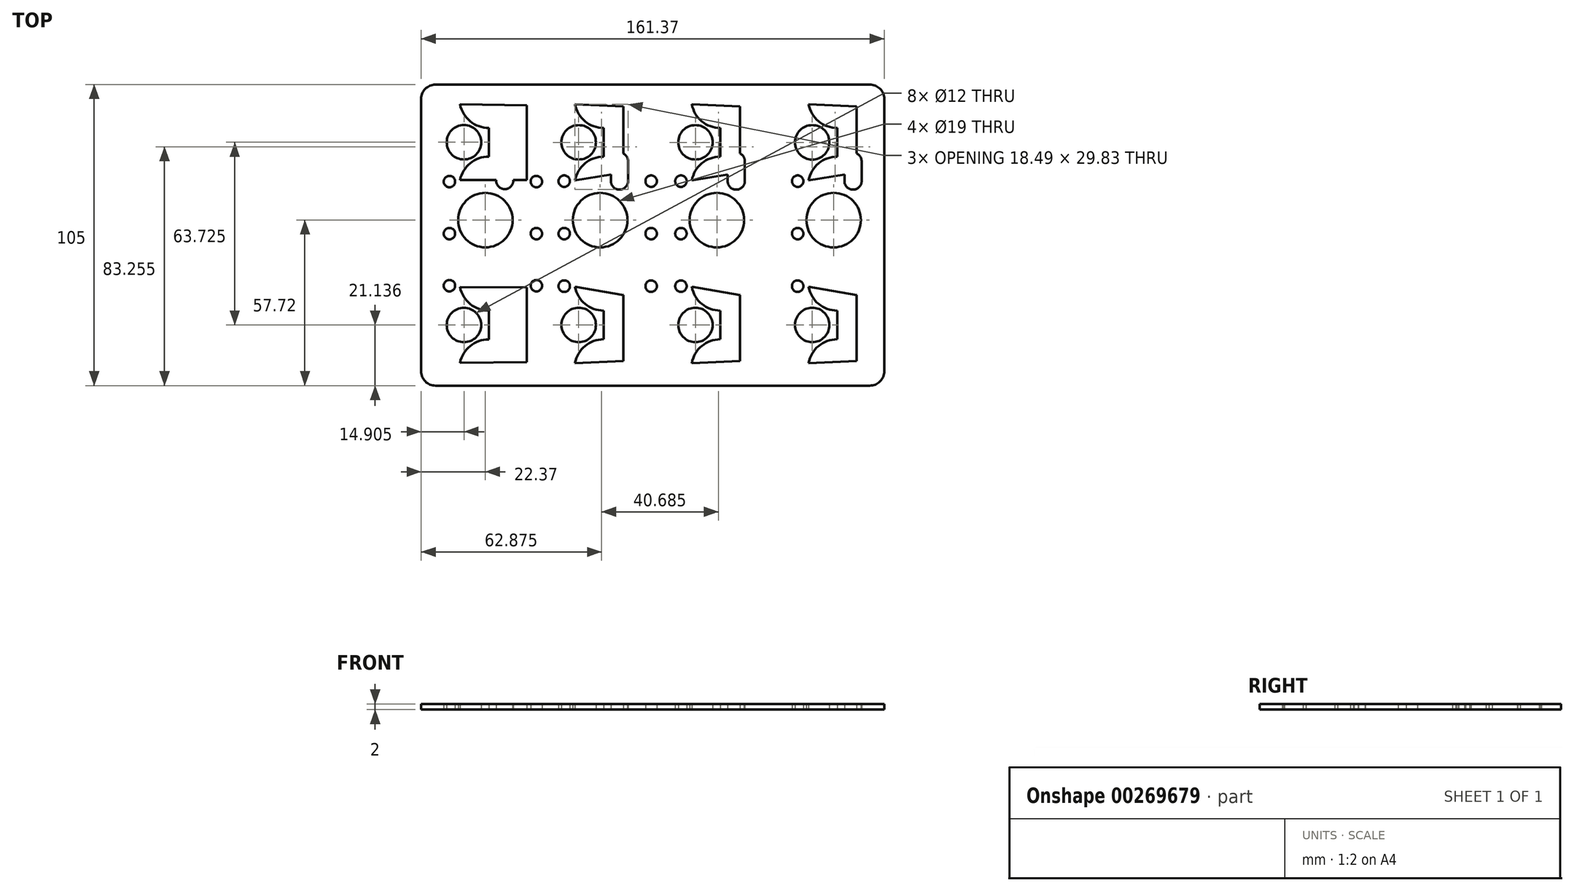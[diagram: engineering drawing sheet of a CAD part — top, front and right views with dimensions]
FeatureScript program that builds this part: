
annotation { "Feature Type Name" : "Feature", "Feature Type Description" : "" }
export const myFeature = defineFeature(function(context is Context, id is Id, definition is map)
    precondition{}
    {
        {
            var Q0;
            Q0=qCreatedBy(makeId("Top.planeOp"),FACE);
            var sketch = newSketch(context, id + "F0", { "sketchPlane" : qUnion([Q0])});
            skLineSegment(sketch, "E0.left", {"start": v(-63.88, 51.14) * mm, "end": v(-63.88, -53.86) * mm});
            skArc(sketch, "E1", {"start": v(-50.35, 44.2) * mm, "mid": v(-46.77, 38.3) * mm, "end": v(-40.26, 36) * mm});
            skLineSegment(sketch, "E2", {"start": v(-40.26, 36) * mm, "end": v(-40.26, 26) * mm});
            skLineSegment(sketch, "E3", {"start": v(-54.06, 31) * mm, "end": v(-19.75, 31) * mm, "construction": true});
            skArc(sketch, "E4.MirrorCS", {"start": v(-50.35, 17.8) * mm, "mid": v(-46.77, 23.7) * mm, "end": v(-40.26, 26) * mm});
            skCircle(sketch, "E5", {"center": v(-44.5, 39.5) * mm, "radius": 1.5 * mm});
            skCircle(sketch, "E6.MirrorC", {"center": v(-44.5, 22.5) * mm, "radius": 1.5 * mm});
            skCircle(sketch, "E7", {"center": v(-48.98, 31) * mm, "radius": 6 * mm});
            skLineSegment(sketch, "E8", {"start": v(-70.35, -0.86) * mm, "end": v(-21.34, -0.86) * mm, "construction": true});
            skCircle(sketch, "E9.MirrorC", {"center": v(-44.5, -24.22) * mm, "radius": 1.5 * mm});
            skArc(sketch, "E10.MirrorCS", {"start": v(-50.35, -19.52) * mm, "mid": v(-46.77, -25.43) * mm, "end": v(-40.26, -27.72) * mm});
            skLineSegment(sketch, "E11.MirrorCS", {"start": v(-40.26, -37.72) * mm, "end": v(-40.26, -27.72) * mm});
            skArc(sketch, "E12.MirrorCS", {"start": v(-50.35, -45.92) * mm, "mid": v(-46.77, -40.02) * mm, "end": v(-40.26, -37.72) * mm});
            skCircle(sketch, "E13.MirrorC", {"center": v(-44.5, -41.22) * mm, "radius": 1.5 * mm});
            skCircle(sketch, "E14.MirrorC", {"center": v(-48.98, -32.72) * mm, "radius": 6 * mm});
            skLineSegment(sketch, "E15", {"start": v(-47.12, -19.26) * mm, "end": v(-47.12, -50.4) * mm, "construction": true});
            skLineSegment(sketch, "E16", {"start": v(-27.05, -19.62) * mm, "end": v(-27.05, -45.62) * mm});
            skLineSegment(sketch, "E17", {"start": v(-27.05, -45.62) * mm, "end": v(-50.35, -45.92) * mm});
            skLineSegment(sketch, "E18", {"start": v(-27.05, -19.62) * mm, "end": v(-50.35, -19.52) * mm});
            skLineSegment(sketch, "E19.MirrorCS", {"start": v(-27.05, 17.9) * mm, "end": v(-50.35, 17.8) * mm});
            skLineSegment(sketch, "E20.MirrorCS", {"start": v(-27.05, 17.9) * mm, "end": v(-27.05, 43.9) * mm});
            skLineSegment(sketch, "E21.MirrorCS", {"start": v(-27.05, 43.9) * mm, "end": v(-50.35, 44.2) * mm});
            skCircle(sketch, "E22", {"center": v(-41.51, 3.86) * mm, "radius": 9.5 * mm});
            skCircle(sketch, "E23", {"center": v(-34.76, 24.59) * mm, "radius": 3 * mm});
            skCircle(sketch, "E24", {"center": v(-34.76, 17.66) * mm, "radius": 3 * mm});
            skLineSegment(sketch, "E25", {"start": v(-31.76, 24.59) * mm, "end": v(-31.76, 17.72) * mm});
            skLineSegment(sketch, "E26", {"start": v(-37.76, 17.66) * mm, "end": v(-37.76, 24.59) * mm});
            skCircle(sketch, "E27", {"center": v(-54.03, -0.86) * mm, "radius": 2 * mm});
            skCircle(sketch, "E28", {"center": v(-54.03, -19.01) * mm, "radius": 2 * mm});
            skCircle(sketch, "E29.MirrorC", {"center": v(-54.03, 17.3) * mm, "radius": 2 * mm});
            skLineSegment(sketch, "E30", {"start": v(-23.88, 51.14) * mm, "end": v(-23.2, 51.14) * mm});
            skLineSegment(sketch, "E31", {"start": v(-23.88, -53.86) * mm, "end": v(-23.34, -53.86) * mm});
            skLineSegment(sketch, "E32", {"start": v(-38.88, -17.7) * mm, "end": v(-38.88, 2.39) * mm, "construction": true});
            skCircle(sketch, "E33.MirrorC", {"center": v(-23.72, -0.86) * mm, "radius": 2 * mm});
            skCircle(sketch, "E34.MirrorC", {"center": v(-23.72, 17.3) * mm, "radius": 2 * mm});
            skCircle(sketch, "E35.MirrorC", {"center": v(-23.72, -19.01) * mm, "radius": 2 * mm});
            skArc(sketch, "E36", {"start": v(-10.25, 44.3) * mm, "mid": v(-6.78, 38.33) * mm, "end": v(-0.27, 35.99) * mm});
            skLineSegment(sketch, "E37", {"start": v(-0.27, 35.99) * mm, "end": v(-0.27, 25.99) * mm});
            skLineSegment(sketch, "E38", {"start": v(-14.06, 30.99) * mm, "end": v(20.24, 30.99) * mm, "construction": true});
            skArc(sketch, "E39.MirrorCS", {"start": v(-10.25, 17.66) * mm, "mid": v(-6.78, 23.65) * mm, "end": v(-0.27, 25.99) * mm});
            skCircle(sketch, "E40", {"center": v(-4.5, 39.49) * mm, "radius": 1.5 * mm});
            skCircle(sketch, "E41.MirrorC", {"center": v(-4.5, 22.49) * mm, "radius": 1.5 * mm});
            skCircle(sketch, "E42", {"center": v(-8.98, 30.99) * mm, "radius": 6 * mm});
            skLineSegment(sketch, "E43", {"start": v(-30.35, -0.86) * mm, "end": v(18.66, -0.86) * mm, "construction": true});
            skCircle(sketch, "E44.MirrorC", {"center": v(-4.5, -24.2) * mm, "radius": 1.5 * mm});
            skArc(sketch, "E45.MirrorCS", {"start": v(-10.25, -19.38) * mm, "mid": v(-6.78, -25.37) * mm, "end": v(-0.27, -27.7) * mm});
            skLineSegment(sketch, "E46.MirrorCS", {"start": v(-0.27, -37.7) * mm, "end": v(-0.27, -27.7) * mm});
            skArc(sketch, "E47.MirrorCS", {"start": v(-10.25, -46.03) * mm, "mid": v(-6.78, -40.05) * mm, "end": v(-0.27, -37.7) * mm});
            skCircle(sketch, "E48.MirrorC", {"center": v(-4.5, -41.2) * mm, "radius": 1.5 * mm});
            skCircle(sketch, "E49.MirrorC", {"center": v(-8.98, -32.7) * mm, "radius": 6 * mm});
            skLineSegment(sketch, "E50", {"start": v(-7.13, -19.44) * mm, "end": v(-7.13, -50.58) * mm, "construction": true});
            skLineSegment(sketch, "E51", {"start": v(6.55, -22.23) * mm, "end": v(6.55, -45.23) * mm});
            skLineSegment(sketch, "E52", {"start": v(6.55, -45.23) * mm, "end": v(-10.25, -46.03) * mm});
            skLineSegment(sketch, "E53", {"start": v(6.55, -22.23) * mm, "end": v(-10.25, -19.38) * mm});
            skLineSegment(sketch, "E54.MirrorCS", {"start": v(6.55, 20.5) * mm, "end": v(-10.25, 17.66) * mm});
            skLineSegment(sketch, "E55.MirrorCS", {"start": v(6.55, 20.5) * mm, "end": v(6.55, 43.5) * mm});
            skLineSegment(sketch, "E56.MirrorCS", {"start": v(6.55, 43.5) * mm, "end": v(-10.25, 44.3) * mm});
            skCircle(sketch, "E57", {"center": v(-1.51, 3.86) * mm, "radius": 9.5 * mm});
            skCircle(sketch, "E58", {"center": v(5.24, 24.4) * mm, "radius": 3 * mm});
            skCircle(sketch, "E59", {"center": v(5.24, 17.48) * mm, "radius": 3 * mm});
            skLineSegment(sketch, "E60", {"start": v(8.24, 24.4) * mm, "end": v(8.24, 17.54) * mm});
            skLineSegment(sketch, "E61", {"start": v(2.24, 17.48) * mm, "end": v(2.24, 24.4) * mm});
            skCircle(sketch, "E62", {"center": v(-14.03, -0.86) * mm, "radius": 2 * mm});
            skCircle(sketch, "E63", {"center": v(-14.03, -19.17) * mm, "radius": 2 * mm});
            skCircle(sketch, "E64.MirrorC", {"center": v(-14.03, 17.45) * mm, "radius": 2 * mm});
            skLineSegment(sketch, "E65", {"start": v(16.12, 51.14) * mm, "end": v(16.8, 51.14) * mm});
            skLineSegment(sketch, "E66", {"start": v(16.12, -53.86) * mm, "end": v(16.66, -53.86) * mm});
            skLineSegment(sketch, "E67", {"start": v(1.12, -28.54) * mm, "end": v(1.12, -8.45) * mm, "construction": true});
            skCircle(sketch, "E68.MirrorC", {"center": v(16.28, -0.86) * mm, "radius": 2 * mm});
            skCircle(sketch, "E69.MirrorC", {"center": v(16.28, 17.45) * mm, "radius": 2 * mm});
            skCircle(sketch, "E70.MirrorC", {"center": v(16.28, -19.17) * mm, "radius": 2 * mm});
            skArc(sketch, "E71", {"start": v(30.44, 44.3) * mm, "mid": v(33.9, 38.33) * mm, "end": v(40.42, 35.99) * mm});
            skLineSegment(sketch, "E72", {"start": v(40.42, 35.99) * mm, "end": v(40.42, 25.99) * mm});
            skLineSegment(sketch, "E73", {"start": v(26.62, 30.99) * mm, "end": v(60.93, 30.99) * mm, "construction": true});
            skArc(sketch, "E74.MirrorCS", {"start": v(30.44, 17.66) * mm, "mid": v(33.9, 23.65) * mm, "end": v(40.42, 25.99) * mm});
            skCircle(sketch, "E75", {"center": v(36.2, 39.49) * mm, "radius": 1.5 * mm});
            skCircle(sketch, "E76.MirrorC", {"center": v(36.2, 22.49) * mm, "radius": 1.5 * mm});
            skCircle(sketch, "E77", {"center": v(31.7, 30.99) * mm, "radius": 6 * mm});
            skLineSegment(sketch, "E78", {"start": v(10.34, -0.86) * mm, "end": v(59.35, -0.86) * mm, "construction": true});
            skCircle(sketch, "E79.MirrorC", {"center": v(36.2, -24.2) * mm, "radius": 1.5 * mm});
            skArc(sketch, "E80.MirrorCS", {"start": v(30.44, -19.38) * mm, "mid": v(33.9, -25.37) * mm, "end": v(40.42, -27.7) * mm});
            skLineSegment(sketch, "E81.MirrorCS", {"start": v(40.42, -37.7) * mm, "end": v(40.42, -27.7) * mm});
            skArc(sketch, "E82.MirrorCS", {"start": v(30.44, -46.03) * mm, "mid": v(33.9, -40.05) * mm, "end": v(40.42, -37.7) * mm});
            skCircle(sketch, "E83.MirrorC", {"center": v(36.2, -41.2) * mm, "radius": 1.5 * mm});
            skCircle(sketch, "E84.MirrorC", {"center": v(31.7, -32.7) * mm, "radius": 6 * mm});
            skLineSegment(sketch, "E85", {"start": v(33.56, -19.44) * mm, "end": v(33.56, -50.58) * mm, "construction": true});
            skLineSegment(sketch, "E86", {"start": v(47.23, -22.23) * mm, "end": v(47.23, -45.23) * mm});
            skLineSegment(sketch, "E87", {"start": v(47.23, -45.23) * mm, "end": v(30.44, -46.03) * mm});
            skLineSegment(sketch, "E88", {"start": v(47.23, -22.23) * mm, "end": v(30.44, -19.38) * mm});
            skLineSegment(sketch, "E89.MirrorCS", {"start": v(47.23, 20.5) * mm, "end": v(30.44, 17.66) * mm});
            skLineSegment(sketch, "E90.MirrorCS", {"start": v(47.23, 20.5) * mm, "end": v(47.23, 43.5) * mm});
            skLineSegment(sketch, "E91.MirrorCS", {"start": v(47.23, 43.5) * mm, "end": v(30.44, 44.3) * mm});
            skCircle(sketch, "E92", {"center": v(39.17, 3.86) * mm, "radius": 9.5 * mm});
            skCircle(sketch, "E93", {"center": v(45.92, 24.4) * mm, "radius": 3 * mm});
            skCircle(sketch, "E94", {"center": v(45.92, 17.48) * mm, "radius": 3 * mm});
            skLineSegment(sketch, "E95", {"start": v(48.92, 24.4) * mm, "end": v(48.92, 17.54) * mm});
            skLineSegment(sketch, "E96", {"start": v(42.92, 17.48) * mm, "end": v(42.92, 24.4) * mm});
            skCircle(sketch, "E97", {"center": v(26.65, -0.86) * mm, "radius": 2 * mm});
            skCircle(sketch, "E98", {"center": v(26.65, -19.17) * mm, "radius": 2 * mm});
            skCircle(sketch, "E99.MirrorC", {"center": v(26.65, 17.45) * mm, "radius": 2 * mm});
            skLineSegment(sketch, "E100", {"start": v(56.8, 51.14) * mm, "end": v(57.49, 51.14) * mm});
            skLineSegment(sketch, "E101", {"start": v(56.8, -53.86) * mm, "end": v(57.34, -53.86) * mm});
            skLineSegment(sketch, "E102", {"start": v(41.8, -17.4) * mm, "end": v(41.8, 2.7) * mm, "construction": true});
            skLineSegment(sketch, "E103.right", {"start": v(97.49, 51.14) * mm, "end": v(97.49, -53.86) * mm});
            skArc(sketch, "E104", {"start": v(71.12, 44.3) * mm, "mid": v(74.6, 38.32) * mm, "end": v(81.1, 35.98) * mm});
            skLineSegment(sketch, "E105", {"start": v(81.1, 35.98) * mm, "end": v(81.1, 25.98) * mm});
            skLineSegment(sketch, "E106", {"start": v(67.3, 30.98) * mm, "end": v(101.62, 30.98) * mm, "construction": true});
            skArc(sketch, "E107.MirrorCS", {"start": v(71.12, 17.66) * mm, "mid": v(74.6, 23.65) * mm, "end": v(81.1, 25.98) * mm});
            skCircle(sketch, "E108", {"center": v(76.88, 39.48) * mm, "radius": 1.5 * mm});
            skCircle(sketch, "E109.MirrorC", {"center": v(76.88, 22.48) * mm, "radius": 1.5 * mm});
            skCircle(sketch, "E110", {"center": v(72.4, 30.98) * mm, "radius": 6 * mm});
            skLineSegment(sketch, "E111", {"start": v(51.02, -0.86) * mm, "end": v(100.03, -0.86) * mm, "construction": true});
            skCircle(sketch, "E112.MirrorC", {"center": v(76.88, -24.2) * mm, "radius": 1.5 * mm});
            skArc(sketch, "E113.MirrorCS", {"start": v(71.12, -19.39) * mm, "mid": v(74.6, -25.37) * mm, "end": v(81.1, -27.7) * mm});
            skLineSegment(sketch, "E114.MirrorCS", {"start": v(81.1, -37.7) * mm, "end": v(81.1, -27.7) * mm});
            skArc(sketch, "E115.MirrorCS", {"start": v(71.12, -46.03) * mm, "mid": v(74.6, -40.05) * mm, "end": v(81.1, -37.7) * mm});
            skCircle(sketch, "E116.MirrorC", {"center": v(76.88, -41.2) * mm, "radius": 1.5 * mm});
            skCircle(sketch, "E117.MirrorC", {"center": v(72.4, -32.7) * mm, "radius": 6 * mm});
            skLineSegment(sketch, "E118", {"start": v(74.24, -19.44) * mm, "end": v(74.24, -50.58) * mm, "construction": true});
            skLineSegment(sketch, "E119", {"start": v(87.92, -22.23) * mm, "end": v(87.92, -45.23) * mm});
            skLineSegment(sketch, "E120", {"start": v(87.92, -45.23) * mm, "end": v(71.12, -46.03) * mm});
            skLineSegment(sketch, "E121", {"start": v(87.92, -22.23) * mm, "end": v(71.12, -19.39) * mm});
            skLineSegment(sketch, "E122.MirrorCS", {"start": v(87.92, 20.5) * mm, "end": v(71.12, 17.66) * mm});
            skLineSegment(sketch, "E123.MirrorCS", {"start": v(87.92, 20.5) * mm, "end": v(87.92, 43.5) * mm});
            skLineSegment(sketch, "E124.MirrorCS", {"start": v(87.92, 43.5) * mm, "end": v(71.12, 44.3) * mm});
            skCircle(sketch, "E125", {"center": v(79.86, 3.86) * mm, "radius": 9.5 * mm});
            skCircle(sketch, "E126", {"center": v(86.6, 24.4) * mm, "radius": 3 * mm});
            skCircle(sketch, "E127", {"center": v(86.6, 17.48) * mm, "radius": 3 * mm});
            skLineSegment(sketch, "E128", {"start": v(89.6, 24.4) * mm, "end": v(89.6, 17.54) * mm});
            skLineSegment(sketch, "E129", {"start": v(83.6, 17.48) * mm, "end": v(83.6, 24.4) * mm});
            skCircle(sketch, "E130", {"center": v(67.33, -0.86) * mm, "radius": 2 * mm});
            skCircle(sketch, "E131", {"center": v(67.33, -19.17) * mm, "radius": 2 * mm});
            skCircle(sketch, "E132.MirrorC", {"center": v(67.33, 17.45) * mm, "radius": 2 * mm});
            skLineSegment(sketch, "E133", {"start": v(97.49, 51.14) * mm, "end": v(98.17, 51.14) * mm});
            skLineSegment(sketch, "E134", {"start": v(97.49, -53.86) * mm, "end": v(98.03, -53.86) * mm});
            skLineSegment(sketch, "E135", {"start": v(98.03, -53.86) * mm, "end": v(98.17, 51.14) * mm});
            skLineSegment(sketch, "E136", {"start": v(82.49, -14.78) * mm, "end": v(82.49, 5.32) * mm, "construction": true});
            skLineSegment(sketch, "E137", {"start": v(-63.88, -53.86) * mm, "end": v(98.03, -53.86) * mm});
            skLineSegment(sketch, "E138", {"start": v(98.17, 51.14) * mm, "end": v(-63.88, 51.14) * mm});
            skLineSegment(sketch, "E139", {"start": v(-48.98, -32.72) * mm, "end": v(72.4, -32.7) * mm, "construction": true});
            skSolve(sketch);
        }
        {
            var Q0;
            {var subQ23=sQuery(id+"F0.wireOp",EDGE,"E0.left");Q0=makeQuery(id+"F0.imprint","IMPRINT",FACE,{"disambiguationData":[TD([[makeQuery(id+"F0.imprint","IMPRINT",EDGE,{"derivedFrom":subQ23}),1.0]])]});}
            extrude(context, id + "F1", {"entities" : qUnion([Q0]), "depth" : 2 * mm});
        }
        {
            var Q0;
            Q0=makeQuery(id+"F1.opExtrude","SWEPT_EDGE",EDGE,{"disambiguationData":[OSD([sQuery(id+"F0.wireOp",EDGE,"E0.left"),sQuery(id+"F0.wireOp",EDGE,"E138")])]});
            var Q1;
            Q1=makeQuery(id+"F1.opExtrude","SWEPT_EDGE",EDGE,{"disambiguationData":[OSD([sQuery(id+"F0.wireOp",EDGE,"E103.right"),sQuery(id+"F0.wireOp",EDGE,"E138")])]});
            var Q2;
            Q2=makeQuery(id+"F1.opExtrude","SWEPT_EDGE",EDGE,{"disambiguationData":[OSD([sQuery(id+"F0.wireOp",EDGE,"E0.left"),sQuery(id+"F0.wireOp",EDGE,"E137")])]});
            var Q3;
            Q3=makeQuery(id+"F1.opExtrude","SWEPT_EDGE",EDGE,{"disambiguationData":[OSD([sQuery(id+"F0.wireOp",EDGE,"E103.right"),sQuery(id+"F0.wireOp",EDGE,"E137")])]});
            fillet(context, id + "F2", {"entities" : qUnion([Q0, Q1, Q2, Q3]), "radius" : 5 * mm, "tangentPropagation" : true, "allowEdgeOverflow" : false});
        }
    });
